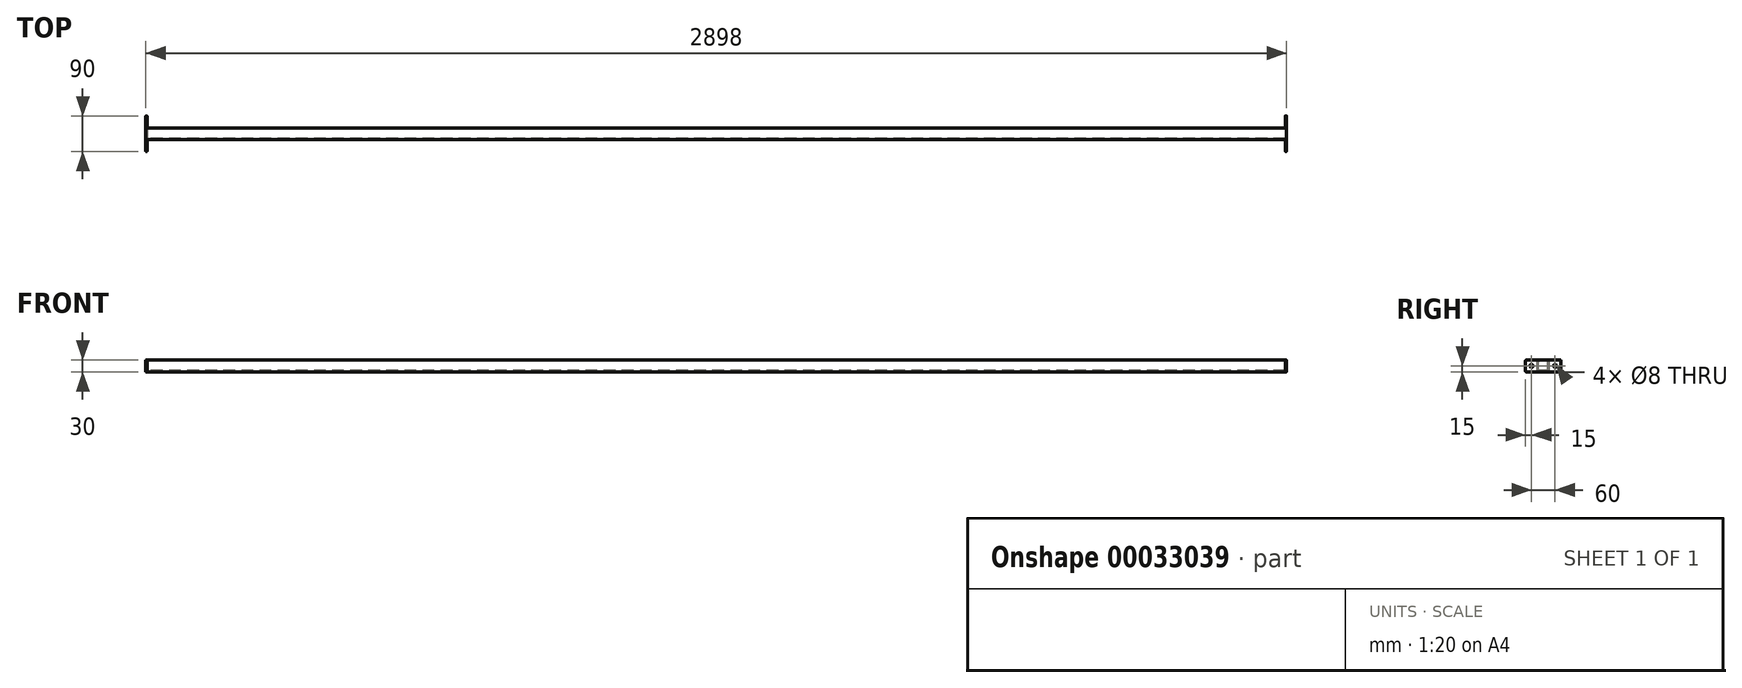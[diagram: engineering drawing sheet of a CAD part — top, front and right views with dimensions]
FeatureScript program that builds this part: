
annotation { "Feature Type Name" : "Feature", "Feature Type Description" : "" }
export const myFeature = defineFeature(function(context is Context, id is Id, definition is map)
    precondition{}
    {
        {
            var Q0;
            Q0=qCreatedBy(makeId("Right.planeOp"),FACE);
            var sketch = newSketch(context, id + "F0", { "sketchPlane" : qUnion([Q0])});
            skLineSegment(sketch, "E0.rect.bottom", {"start": v(12, -15) * mm, "end": v(-12, -15) * mm});
            skLineSegment(sketch, "E0.rect.top", {"start": v(12, 15) * mm, "end": v(-12, 15) * mm});
            skLineSegment(sketch, "E0.rect.left", {"start": v(15, -12) * mm, "end": v(15, 12) * mm});
            skLineSegment(sketch, "E0.rect.right", {"start": v(-15, -12) * mm, "end": v(-15, 12) * mm});
            skPoint(sketch, "E0.rect.middle", {"position": v(0, 0) * mm});
            skPoint(sketch, "E1.visualSharp", {"position": v(-15, 15) * mm});
            skArc(sketch, "E1.filletArc", {"start": v(-12, 15) * mm, "mid": v(-14.12, 14.12) * mm, "end": v(-15, 12) * mm});
            skPoint(sketch, "E2.visualSharp", {"position": v(15, 15) * mm});
            skArc(sketch, "E2.filletArc", {"start": v(15, 12) * mm, "mid": v(14.12, 14.12) * mm, "end": v(12, 15) * mm});
            skPoint(sketch, "E3.visualSharp", {"position": v(15, -15) * mm});
            skArc(sketch, "E3.filletArc", {"start": v(12, -15) * mm, "mid": v(14.12, -14.12) * mm, "end": v(15, -12) * mm});
            skPoint(sketch, "E4.visualSharp", {"position": v(-15, -15) * mm});
            skArc(sketch, "E4.filletArc", {"start": v(-15, -12) * mm, "mid": v(-14.12, -14.12) * mm, "end": v(-12, -15) * mm});
            skLineSegment(sketch, "E5.0", {"start": v(10, -12) * mm, "end": v(-10, -12) * mm});
            skLineSegment(sketch, "E5.1", {"start": v(12, -10) * mm, "end": v(12, 10) * mm});
            skLineSegment(sketch, "E5.2", {"start": v(10, 12) * mm, "end": v(-10, 12) * mm});
            skLineSegment(sketch, "E5.3", {"start": v(-12, -10) * mm, "end": v(-12, 10) * mm});
            skArc(sketch, "E6.filletArc", {"start": v(-10, 12) * mm, "mid": v(-11.41, 11.41) * mm, "end": v(-12, 10) * mm});
            skArc(sketch, "E7.filletArc", {"start": v(12, 10) * mm, "mid": v(11.41, 11.41) * mm, "end": v(10, 12) * mm});
            skArc(sketch, "E8.filletArc", {"start": v(10, -12) * mm, "mid": v(11.41, -11.41) * mm, "end": v(12, -10) * mm});
            skArc(sketch, "E9.filletArc", {"start": v(-12, -10) * mm, "mid": v(-11.41, -11.41) * mm, "end": v(-10, -12) * mm});
            skSolve(sketch);
        }
        {
            var Q0;
            Q0=qCreatedBy(makeId("Right.planeOp"),FACE);
            cPlane(context, id + "F1", {"entities" : qUnion([Q0]), "cplaneType" : CPlaneType.OFFSET, "offset" : 2898 * mm, "width" : 150 * mm, "height" : 150 * mm});
        }
        {
            var Q0;
            Q0 = qSketchRegion(id + "F0", true);
            var Q1;
            Q1=qCreatedBy(id+"F1.planeOp",FACE);
            extrude(context, id + "F2", {"entities" : qUnion([Q0]), "endBound" : BoundingType.UP_TO_SURFACE, "endBoundEntityFace" : qUnion([Q1]), "depth" : 25 * mm});
        }
        {
            var Q0;
            Q0=qCreatedBy(makeId("Right.planeOp"),FACE);
            var sketch = newSketch(context, id + "F3", { "sketchPlane" : qUnion([Q0])});
            skLineSegment(sketch, "E10.bottom", {"start": v(43, 15) * mm, "end": v(-43, 15) * mm});
            skLineSegment(sketch, "E10.top", {"start": v(43, -15) * mm, "end": v(-43, -15) * mm});
            skLineSegment(sketch, "E10.left", {"start": v(45, 13) * mm, "end": v(45, -13) * mm});
            skLineSegment(sketch, "E10.right", {"start": v(-45, 13) * mm, "end": v(-45, -13) * mm});
            skPoint(sketch, "E11.visualSharp", {"position": v(45, 15) * mm});
            skArc(sketch, "E11.filletArc", {"start": v(45, 13) * mm, "mid": v(44.41, 14.41) * mm, "end": v(43, 15) * mm});
            skPoint(sketch, "E12.visualSharp", {"position": v(45, -15) * mm});
            skArc(sketch, "E12.filletArc", {"start": v(43, -15) * mm, "mid": v(44.41, -14.41) * mm, "end": v(45, -13) * mm});
            skPoint(sketch, "E13.visualSharp", {"position": v(-45, 15) * mm});
            skArc(sketch, "E13.filletArc", {"start": v(-43, 15) * mm, "mid": v(-44.41, 14.41) * mm, "end": v(-45, 13) * mm});
            skPoint(sketch, "E14.visualSharp", {"position": v(-45, -15) * mm});
            skArc(sketch, "E14.filletArc", {"start": v(-45, -13) * mm, "mid": v(-44.41, -14.41) * mm, "end": v(-43, -15) * mm});
            skPoint(sketch, "E15", {"position": v(30, 0) * mm});
            skPoint(sketch, "E16", {"position": v(-30, 0) * mm});
            skSolve(sketch);
        }
        {
            var Q0;
            Q0 = qSketchRegion(id + "F3", true);
            extrude(context, id + "F4", {"entities" : qUnion([Q0]), "operationType" : NewBodyOperationType.ADD, "depth" : 3 * mm});
        }
        {
            var Q0;
            Q0=sQuery(id+"F3.wireOp",VERTEX,"E15");
            var Q1;
            Q1=sQuery(id+"F3.wireOp",VERTEX,"E16");
            var Q2;
            Q2=makeQuery(id+"F2.opExtrude","SWEPT_BODY",BODY,{"disambiguationData":[OSD([sQuery(id+"F0.wireOp",EDGE,"E0.rect.bottom"),sQuery(id+"F0.wireOp",EDGE,"E0.rect.top"),sQuery(id+"F0.wireOp",EDGE,"E0.rect.left"),sQuery(id+"F0.wireOp",EDGE,"E0.rect.right"),sQuery(id+"F0.wireOp",EDGE,"E1.filletArc"),sQuery(id+"F0.wireOp",EDGE,"E2.filletArc"),sQuery(id+"F0.wireOp",EDGE,"E3.filletArc"),sQuery(id+"F0.wireOp",EDGE,"E4.filletArc"),sQuery(id+"F0.wireOp",EDGE,"E5.0"),sQuery(id+"F0.wireOp",EDGE,"E5.1"),sQuery(id+"F0.wireOp",EDGE,"E5.2"),sQuery(id+"F0.wireOp",EDGE,"E5.3"),sQuery(id+"F0.wireOp",EDGE,"E6.filletArc"),sQuery(id+"F0.wireOp",EDGE,"E7.filletArc"),sQuery(id+"F0.wireOp",EDGE,"E8.filletArc"),sQuery(id+"F0.wireOp",EDGE,"E9.filletArc")])]});
            hole(context, id + "F5", {"style" : HoleStyle.SIMPLE, "holeDiameter" : 8 * mm, "endStyle" : HoleEndStyle.THROUGH, "oppositeDirection" : true, "locations" : qUnion([Q0, Q1]), "scope" : qUnion([Q2])});
        }
        {
            var Q0;
            Q0=qCreatedBy(id+"F1.planeOp",FACE);
            var sketch = newSketch(context, id + "F6", { "sketchPlane" : qUnion([Q0])});
            skLineSegment(sketch, "E17.0", {"start": v(43, 15) * mm, "end": v(-43, 15) * mm});
            skLineSegment(sketch, "E18.0", {"start": v(45, 13) * mm, "end": v(45, -13) * mm});
            skCircle(sketch, "E19.0", {"center": v(30, 0) * mm, "radius": 4 * mm});
            skCircle(sketch, "E20.0", {"center": v(-30, 0) * mm, "radius": 4 * mm});
            skLineSegment(sketch, "E21.0", {"start": v(-45, 13) * mm, "end": v(-45, -13) * mm});
            skLineSegment(sketch, "E22.0", {"start": v(43, -15) * mm, "end": v(-43, -15) * mm});
            skArc(sketch, "E23.0", {"start": v(-43, 15) * mm, "mid": v(-44.41, 14.41) * mm, "end": v(-45, 13) * mm});
            skArc(sketch, "E24.0", {"start": v(45, 13) * mm, "mid": v(44.41, 14.41) * mm, "end": v(43, 15) * mm});
            skArc(sketch, "E25.0", {"start": v(43, -15) * mm, "mid": v(44.41, -14.41) * mm, "end": v(45, -13) * mm});
            skArc(sketch, "E26.0", {"start": v(-45, -13) * mm, "mid": v(-44.41, -14.41) * mm, "end": v(-43, -15) * mm});
            skSolve(sketch);
        }
        {
            var Q0;
            Q0 = qSketchRegion(id + "F6", true);
            extrude(context, id + "F7", {"entities" : qUnion([Q0]), "operationType" : NewBodyOperationType.ADD, "oppositeDirection" : true, "depth" : 3 * mm});
        }
    });
